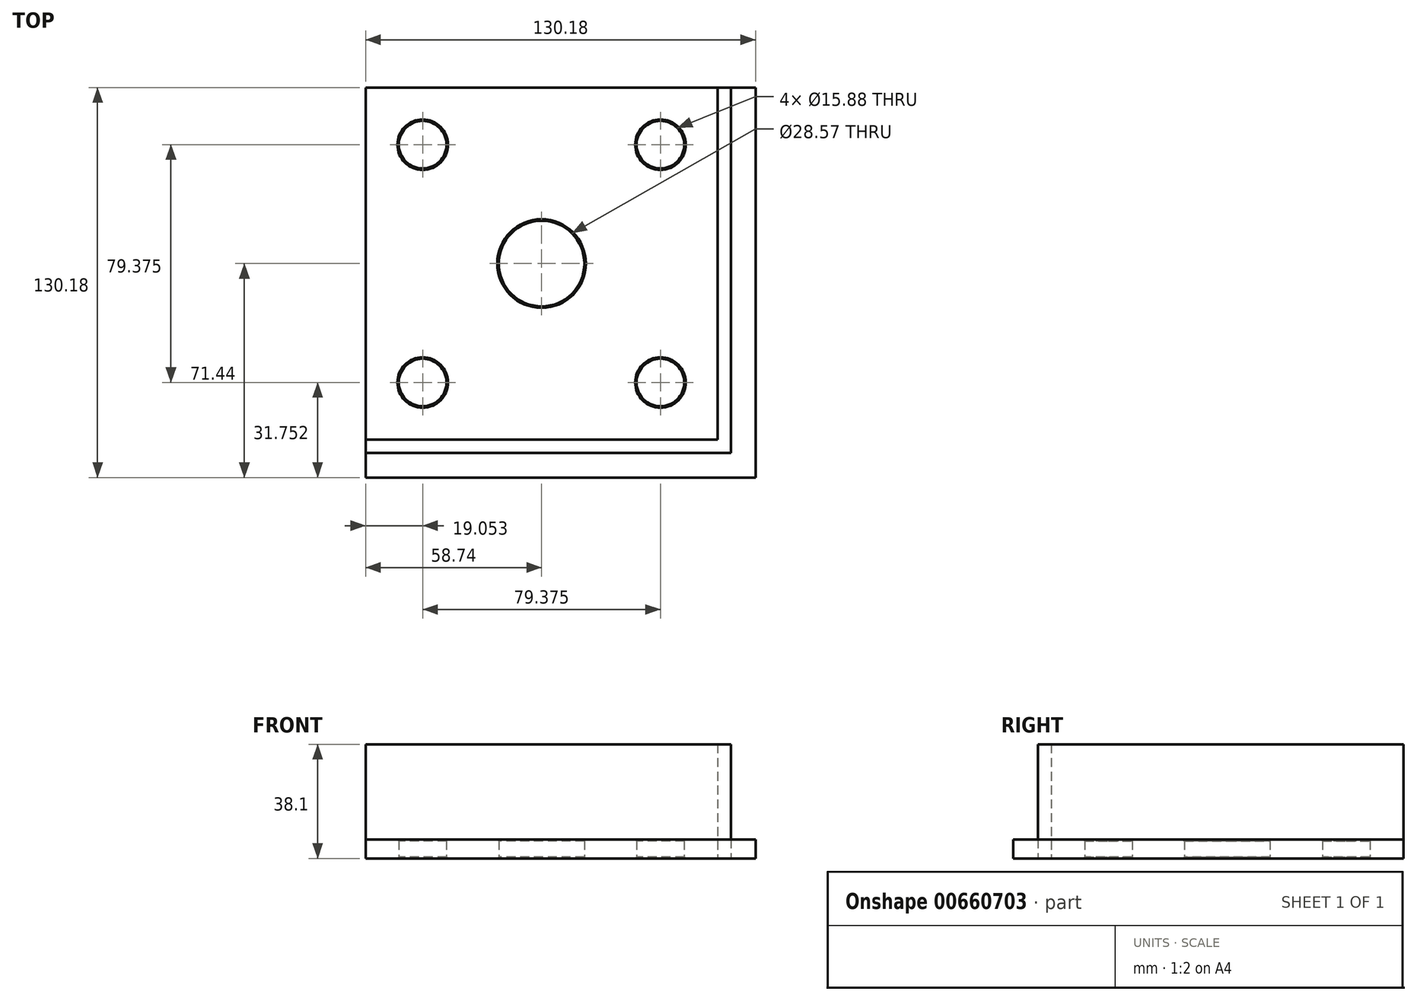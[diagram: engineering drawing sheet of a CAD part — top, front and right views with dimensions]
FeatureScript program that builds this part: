
annotation { "Feature Type Name" : "Feature", "Feature Type Description" : "" }
export const myFeature = defineFeature(function(context is Context, id is Id, definition is map)
    precondition{}
    {
        {
            var Q0;
            Q0=qCreatedBy(makeId("Top.planeOp"),FACE);
            var sketch = newSketch(context, id + "F0", { "sketchPlane" : qUnion([Q0])});
            skLineSegment(sketch, "E0.bottom", {"start": v(-58.74, 58.74) * mm, "end": v(58.74, 58.74) * mm});
            skLineSegment(sketch, "E0.top", {"start": v(-58.74, -58.74) * mm, "end": v(58.74, -58.74) * mm});
            skLineSegment(sketch, "E0.left", {"start": v(-58.74, 58.74) * mm, "end": v(-58.74, -58.74) * mm});
            skLineSegment(sketch, "E0.right", {"start": v(58.74, 58.74) * mm, "end": v(58.74, -58.74) * mm});
            skPoint(sketch, "E0.middle", {"position": v(0, 0) * mm});
            skCircle(sketch, "E1", {"center": v(0, 0) * mm, "radius": 14.29 * mm});
            skCircle(sketch, "E2", {"center": v(-39.69, 39.69) * mm, "radius": 7.94 * mm});
            skCircle(sketch, "E3.1.0", {"center": v(-39.69, -39.69) * mm, "radius": 7.94 * mm});
            skCircle(sketch, "E3.2.0", {"center": v(39.69, -39.69) * mm, "radius": 7.94 * mm});
            skCircle(sketch, "E3.3.0", {"center": v(39.69, 39.69) * mm, "radius": 7.94 * mm});
            skLineSegment(sketch, "E4.bottom", {"start": v(-58.74, 58.74) * mm, "end": v(63.24, 58.74) * mm});
            skLineSegment(sketch, "E4.top", {"start": v(-58.74, -63.24) * mm, "end": v(63.24, -63.24) * mm});
            skLineSegment(sketch, "E4.left", {"start": v(-58.74, 58.74) * mm, "end": v(-58.74, -63.24) * mm});
            skLineSegment(sketch, "E4.right", {"start": v(63.24, 58.74) * mm, "end": v(63.24, -63.24) * mm});
            skLineSegment(sketch, "E5.top", {"start": v(-58.74, -71.44) * mm, "end": v(71.44, -71.44) * mm});
            skLineSegment(sketch, "E5.right", {"start": v(71.44, 58.74) * mm, "end": v(71.44, -71.44) * mm});
            skLineSegment(sketch, "E6", {"start": v(58.74, 58.74) * mm, "end": v(63.24, 58.74) * mm});
            skLineSegment(sketch, "E7", {"start": v(-58.74, -58.74) * mm, "end": v(-58.74, -63.24) * mm});
            skLineSegment(sketch, "E8", {"start": v(-58.74, -63.24) * mm, "end": v(-58.74, -71.44) * mm});
            skLineSegment(sketch, "E9", {"start": v(63.24, 58.74) * mm, "end": v(71.44, 58.74) * mm});
            skSolve(sketch);
        }
        {
            var Q0;
            {var subQ1=sQuery(id+"F0.wireOp",EDGE,"E0.top");Q0=makeQuery(id+"F0.imprint","IMPRINT",FACE,{"disambiguationData":[TD([[makeQuery(id+"F0.imprint","IMPRINT",EDGE,{"derivedFrom":subQ1}),1.0]])]});}
            var Q1;
            {var subQ3=sQuery(id+"F0.wireOp",EDGE,"E0.top");Q1=makeQuery(id+"F0.imprint","IMPRINT",FACE,{"disambiguationData":[TD([[makeQuery(id+"F0.imprint","IMPRINT",EDGE,{"derivedFrom":subQ3}),-1.0]])]});}
            var Q2;
            {var subQ4=sQuery(id+"F0.wireOp",EDGE,"E4.top");Q2=makeQuery(id+"F0.imprint","IMPRINT",FACE,{"disambiguationData":[TD([[makeQuery(id+"F0.imprint","IMPRINT",EDGE,{"derivedFrom":subQ4}),-1.0]])]});}
            extrude(context, id + "F1", {"entities" : qUnion([Q0, Q1, Q2]), "depth" : 6.35 * mm, "offsetDistance" : 25.4 * mm});
        }
        {
            var Q0;
            Q0=makeQuery(id+"F0.imprint","IMPRINT",FACE,{"disambiguationData":[TD([[makeQuery(id+"F0.imprint","IMPRINT",EDGE,{"derivedFrom":sQuery(id+"F0.wireOp",EDGE,"E0.top")}),-1.0]])]});
            extrude(context, id + "F2", {"entities" : qUnion([Q0]), "depth" : 38.1 * mm, "offsetDistance" : 25.4 * mm});
        }
        {
            var Q0;
            Q0=makeQuery(id+"F1.opExtrude","CAP_EDGE",EDGE,{"disambiguationData":[OSD([sQuery(id+"F0.wireOp",EDGE,"E3.2.0")])],"isStart":true});
            var Q1;
            Q1=makeQuery(id+"F1.opExtrude","CAP_EDGE",EDGE,{"disambiguationData":[OSD([sQuery(id+"F0.wireOp",EDGE,"E3.1.0")])],"isStart":true});
            var Q2;
            Q2=makeQuery(id+"F1.opExtrude","CAP_EDGE",EDGE,{"disambiguationData":[OSD([sQuery(id+"F0.wireOp",EDGE,"E2")])],"isStart":true});
            var Q3;
            Q3=makeQuery(id+"F1.opExtrude","CAP_EDGE",EDGE,{"disambiguationData":[OSD([sQuery(id+"F0.wireOp",EDGE,"E3.3.0")])],"isStart":true});
            var Q4;
            Q4=makeQuery(id+"F1.opExtrude","CAP_EDGE",EDGE,{"disambiguationData":[OSD([sQuery(id+"F0.wireOp",EDGE,"E1")])],"isStart":true});
            chamfer(context, id + "F3", {"entities" : qUnion([Q0, Q1, Q2, Q3, Q4]), "width" : 0.5 * mm, "tangentPropagation" : true});
        }
        {
            var Q0;
            Q0=makeQuery(id+"F1.opExtrude","CAP_EDGE",EDGE,{"disambiguationData":[OSD([sQuery(id+"F0.wireOp",EDGE,"E2")])],"isStart":false});
            var Q1;
            Q1=makeQuery(id+"F1.opExtrude","CAP_EDGE",EDGE,{"disambiguationData":[OSD([sQuery(id+"F0.wireOp",EDGE,"E3.3.0")])],"isStart":false});
            var Q2;
            Q2=makeQuery(id+"F1.opExtrude","CAP_EDGE",EDGE,{"disambiguationData":[OSD([sQuery(id+"F0.wireOp",EDGE,"E1")])],"isStart":false});
            var Q3;
            Q3=makeQuery(id+"F1.opExtrude","CAP_EDGE",EDGE,{"disambiguationData":[OSD([sQuery(id+"F0.wireOp",EDGE,"E3.2.0")])],"isStart":false});
            var Q4;
            Q4=makeQuery(id+"F1.opExtrude","CAP_EDGE",EDGE,{"disambiguationData":[OSD([sQuery(id+"F0.wireOp",EDGE,"E3.1.0")])],"isStart":false});
            chamfer(context, id + "F4", {"entities" : qUnion([Q0, Q1, Q2, Q3, Q4]), "width" : 0.5 * mm, "tangentPropagation" : true});
        }
    });
